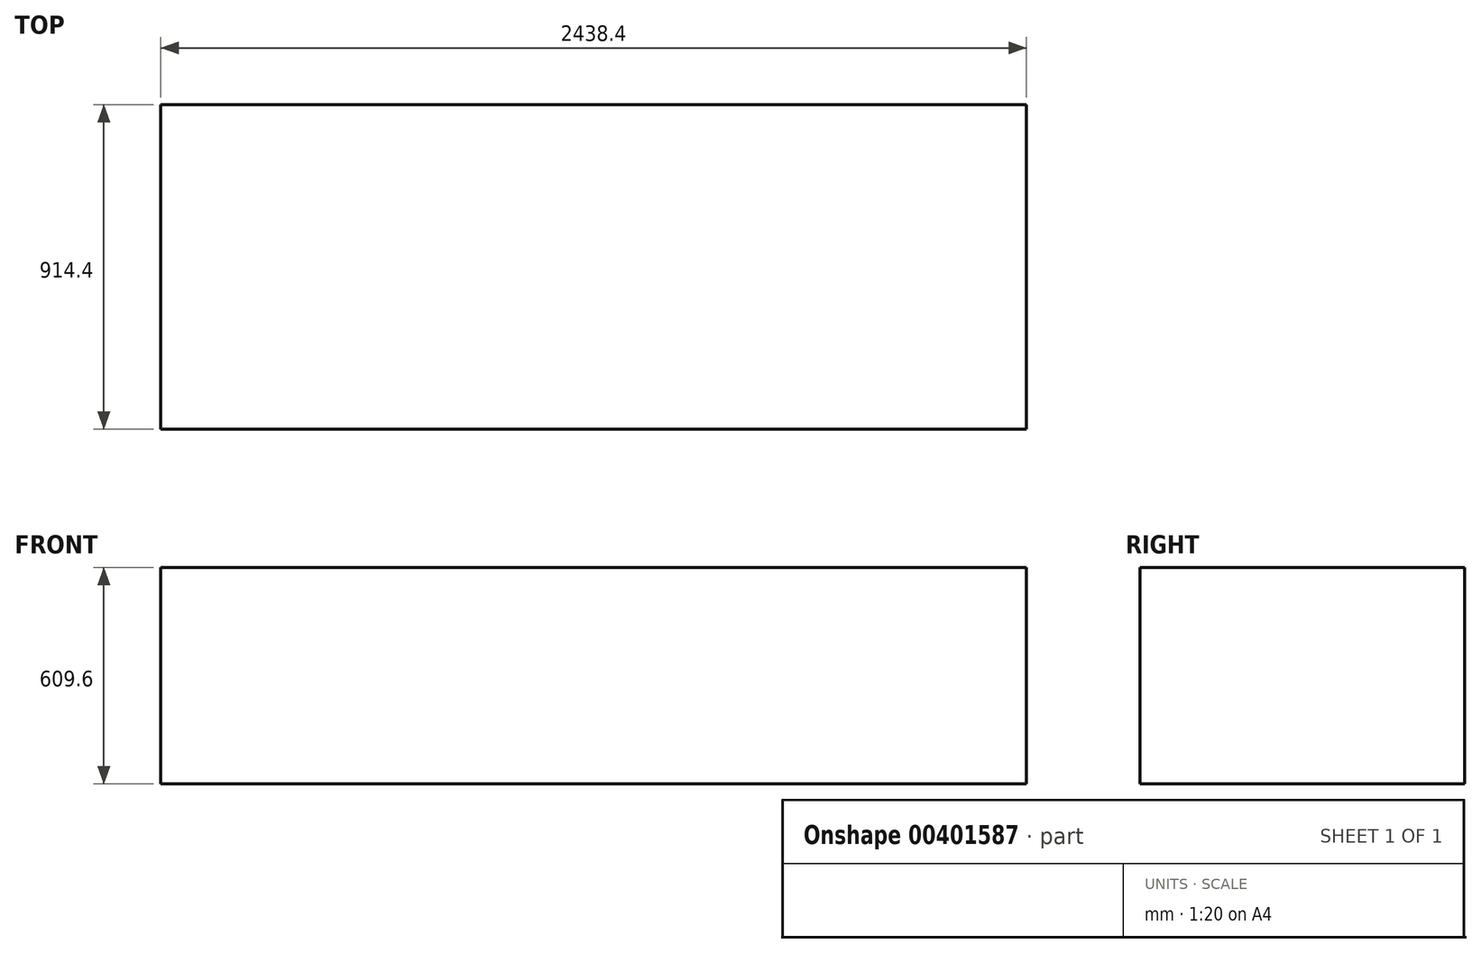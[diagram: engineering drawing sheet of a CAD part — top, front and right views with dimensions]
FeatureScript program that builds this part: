
annotation { "Feature Type Name" : "Feature", "Feature Type Description" : "" }
export const myFeature = defineFeature(function(context is Context, id is Id, definition is map)
    precondition{}
    {
        {
            var Q0;
            Q0=qCreatedBy(makeId("Front.planeOp"),FACE);
            var sketch = newSketch(context, id + "F0", { "sketchPlane" : qUnion([Q0])});
            skLineSegment(sketch, "E0.bottom", {"start": v(-1219.2, 0) * mm, "end": v(1219.2, 0) * mm});
            skLineSegment(sketch, "E0.top", {"start": v(-1219.2, 609.6) * mm, "end": v(1219.2, 609.6) * mm});
            skLineSegment(sketch, "E0.left", {"start": v(-1219.2, 0) * mm, "end": v(-1219.2, 609.6) * mm});
            skLineSegment(sketch, "E0.right", {"start": v(1219.2, 0) * mm, "end": v(1219.2, 609.6) * mm});
            skSolve(sketch);
        }
        {
            var Q0;
            Q0 = qSketchRegion(id + "F0", true);
            extrude(context, id + "F1", {"entities" : qUnion([Q0]), "oppositeDirection" : true, "depth" : 914.4 * mm});
        }
    });
